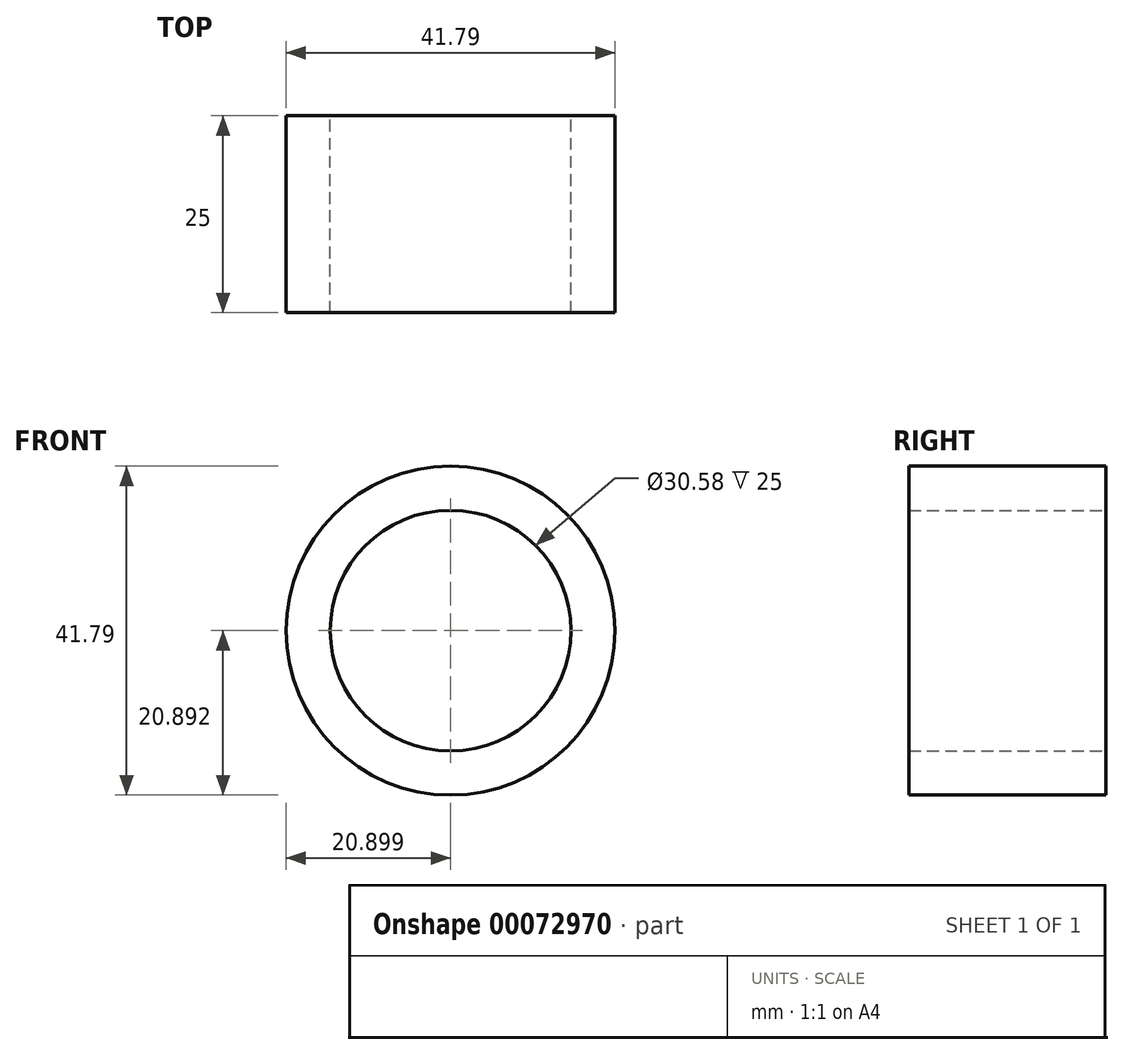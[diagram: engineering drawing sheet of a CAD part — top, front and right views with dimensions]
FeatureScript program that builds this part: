
annotation { "Feature Type Name" : "Feature", "Feature Type Description" : "" }
export const myFeature = defineFeature(function(context is Context, id is Id, definition is map)
    precondition{}
    {
        {
            var Q0;
            Q0=qCreatedBy(makeId("Front.planeOp"),FACE);
            var sketch = newSketch(context, id + "F0", { "sketchPlane" : qUnion([Q0])});
            skCircle(sketch, "E0", {"center": v(-49.38, -4.16) * mm, "radius": 15.29 * mm});
            skCircle(sketch, "E1", {"center": v(-49.38, -4.16) * mm, "radius": 20.9 * mm});
            skSolve(sketch);
        }
        {
            var Q0;
            Q0 = qSketchRegion(id + "F0", true);
            extrude(context, id + "F1", {"entities" : qUnion([Q0]), "depth" : 25 * mm});
        }
    });
